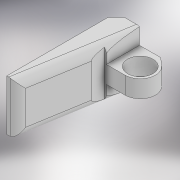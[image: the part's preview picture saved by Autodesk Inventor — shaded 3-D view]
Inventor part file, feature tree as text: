
AUTODESK INVENTOR PART (.ipt)
format: ipt  version: 2022 (Build 260153000, 153)  size: 154,624 bytes
history: native  units: mm
features: extrude x2, sketch x1, fillet x1, chamfer x1
ambient origin geometry x8: Origin, YZ Plane, XZ Plane, XY Plane, X Axis, Y Axis, Z Axis, Center Point
bodies: Solid1 (feature_tree)
feature tree (5):
  sketch  "Sketch1"  dims[d0=5.5mm d1=5.0mm d2=2.5mm d3=10.5mm d4=7.2mm d5=6.0mm d6=4.1mm d7=0.0mm d8=12.0mm d9=0.0mm d10=2.0mm d11=2.0mm d12=2.0mm d13=45.0deg d14=4.23mm]
  extrude  "Extrusion1"  Depth=5.0mm
  extrude  "Extrusion2"  Depth=2.0mm
  fillet  "Fillet1"  Radius=10.5mm
  chamfer  "Chamfer1"  Distance=7.2mm
